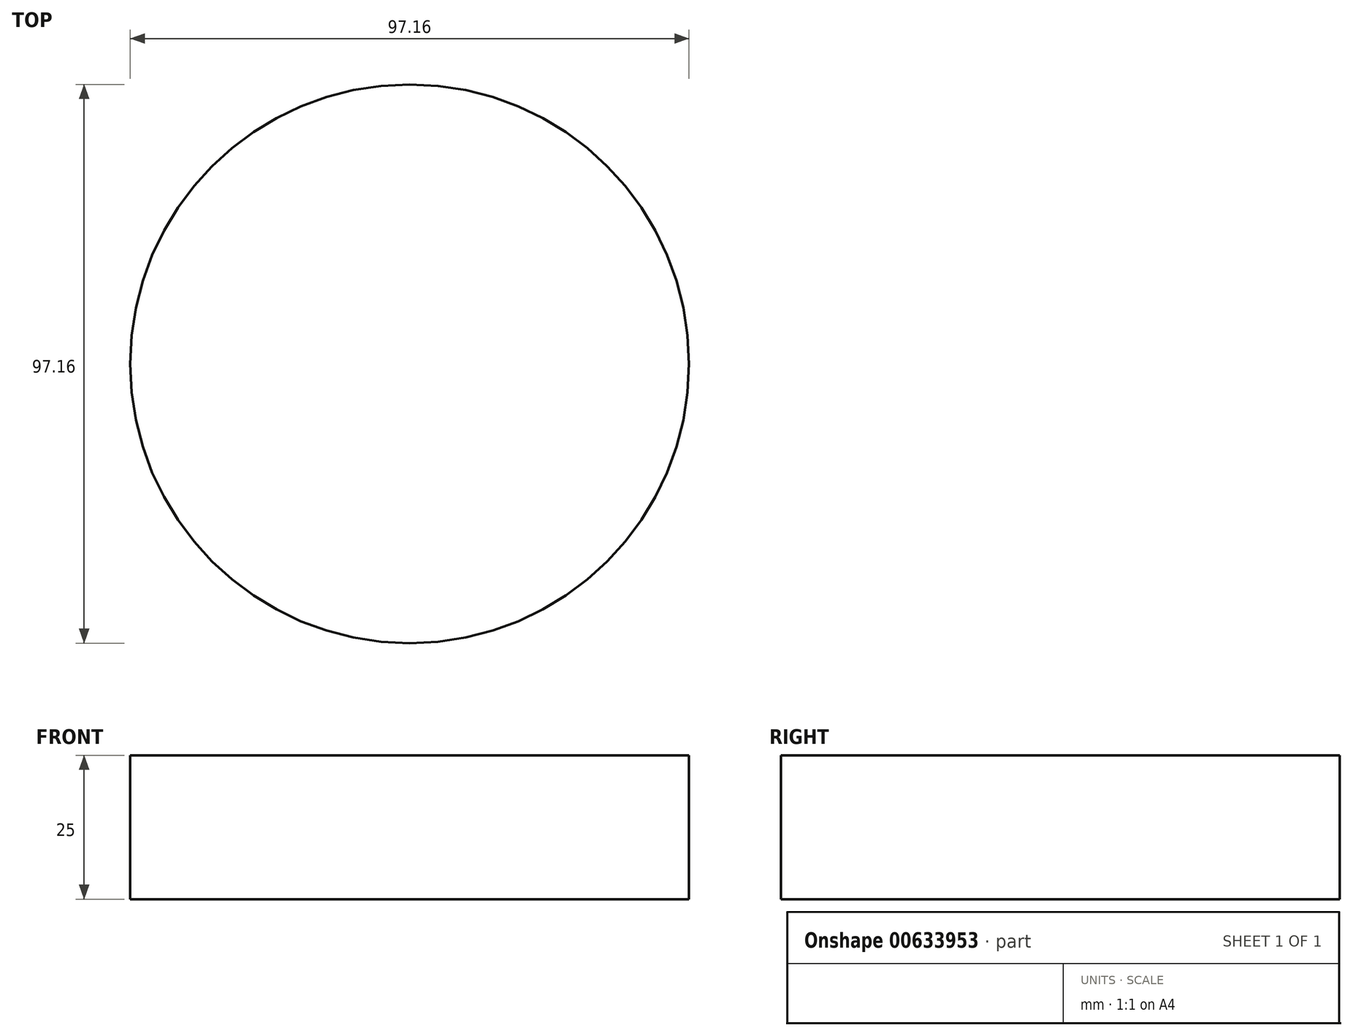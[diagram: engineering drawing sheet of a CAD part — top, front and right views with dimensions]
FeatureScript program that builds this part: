
annotation { "Feature Type Name" : "Feature", "Feature Type Description" : "" }
export const myFeature = defineFeature(function(context is Context, id is Id, definition is map)
    precondition{}
    {
        {
            var Q0;
            Q0=qCreatedBy(makeId("Top.planeOp"),FACE);
            var sketch = newSketch(context, id + "F0", { "sketchPlane" : qUnion([Q0])});
            skCircle(sketch, "E0", {"center": v(0, 0) * mm, "radius": 48.58 * mm});
            skSolve(sketch);
        }
        {
            var Q0;
            Q0=makeQuery(id+"F0.imprint","IMPRINT",FACE,{"disambiguationData":[TD([[makeQuery(id+"F0.imprint","IMPRINT",EDGE,{"derivedFrom":sQuery(id+"F0.wireOp",EDGE,"E0")}),1.0]])]});
            extrude(context, id + "F1", {"entities" : qUnion([Q0]), "depth" : 25 * mm, "offsetDistance" : 25 * mm});
        }
    });
